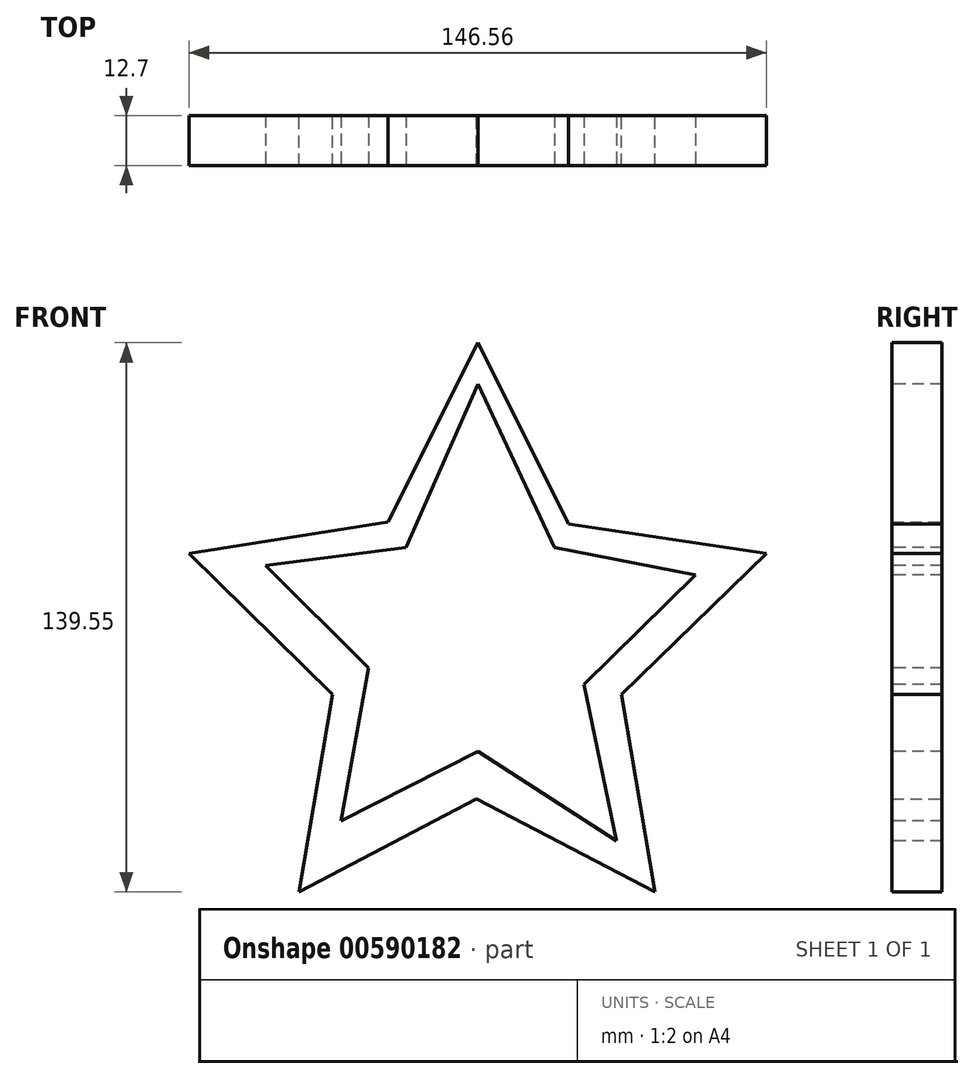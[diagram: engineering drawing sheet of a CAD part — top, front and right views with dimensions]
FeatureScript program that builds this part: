
annotation { "Feature Type Name" : "Feature", "Feature Type Description" : "" }
export const myFeature = defineFeature(function(context is Context, id is Id, definition is map)
    precondition{}
    {
        {
            var Q0;
            Q0=qCreatedBy(makeId("Front.planeOp"),FACE);
            var sketch = newSketch(context, id + "F0", { "sketchPlane" : qUnion([Q0])});
            skLineSegment(sketch, "E0", {"start": v(-16.38, 0) * mm, "end": v(-39.2, -45.54) * mm});
            skLineSegment(sketch, "E1", {"start": v(-39.2, -45.54) * mm, "end": v(-89.66, -53.55) * mm});
            skLineSegment(sketch, "E2", {"start": v(-89.66, -53.55) * mm, "end": v(-53.23, -89.36) * mm});
            skLineSegment(sketch, "E3", {"start": v(-53.23, -89.36) * mm, "end": v(-61.75, -139.55) * mm});
            skLineSegment(sketch, "E4", {"start": v(-61.75, -139.55) * mm, "end": v(-16.67, -115.9) * mm});
            skLineSegment(sketch, "E5", {"start": v(-16.67, -115.9) * mm, "end": v(28.66, -139.55) * mm});
            skLineSegment(sketch, "E6", {"start": v(28.66, -139.55) * mm, "end": v(20.14, -89.36) * mm});
            skLineSegment(sketch, "E7", {"start": v(20.14, -89.36) * mm, "end": v(56.9, -53.55) * mm});
            skLineSegment(sketch, "E8", {"start": v(56.9, -53.55) * mm, "end": v(6.62, -46.04) * mm});
            skLineSegment(sketch, "E9", {"start": v(6.62, -46.04) * mm, "end": v(-16.38, 0) * mm});
            skSolve(sketch);
        }
        {
            var Q0;
            Q0=qSketchRegion(id+"F0",true);
            extrude(context, id + "F1", {"entities" : qUnion([Q0]), "depth" : 12.7 * mm, "offsetDistance" : 25.4 * mm});
        }
        {
            var Q0;
            Q0=makeQuery(id+"F1.opExtrude","CAP_FACE",FACE,{"disambiguationData":[OSD([sQuery(id+"F0.wireOp",EDGE,"E0"),sQuery(id+"F0.wireOp",EDGE,"E1"),sQuery(id+"F0.wireOp",EDGE,"E2"),sQuery(id+"F0.wireOp",EDGE,"E3"),sQuery(id+"F0.wireOp",EDGE,"E4"),sQuery(id+"F0.wireOp",EDGE,"E5"),sQuery(id+"F0.wireOp",EDGE,"E6"),sQuery(id+"F0.wireOp",EDGE,"E7"),sQuery(id+"F0.wireOp",EDGE,"E8"),sQuery(id+"F0.wireOp",EDGE,"E9")])],"isStart":false});
            var sketch = newSketch(context, id + "F2", { "sketchPlane" : qUnion([Q0])});
            skLineSegment(sketch, "E10", {"start": v(-16.27, -10.52) * mm, "end": v(-34.59, -52.01) * mm});
            skLineSegment(sketch, "E11", {"start": v(-34.59, -52.01) * mm, "end": v(-70.34, -56.65) * mm});
            skLineSegment(sketch, "E12", {"start": v(-70.34, -56.65) * mm, "end": v(-44.07, -82.69) * mm});
            skLineSegment(sketch, "E13", {"start": v(-44.07, -82.69) * mm, "end": v(-51.14, -121.53) * mm});
            skLineSegment(sketch, "E14", {"start": v(-51.14, -121.53) * mm, "end": v(-16.38, -103.87) * mm});
            skLineSegment(sketch, "E15", {"start": v(-16.38, -103.87) * mm, "end": v(18.82, -126.6) * mm});
            skLineSegment(sketch, "E16", {"start": v(18.82, -126.6) * mm, "end": v(10.65, -86.88) * mm});
            skLineSegment(sketch, "E17", {"start": v(10.65, -86.88) * mm, "end": v(38.9, -59.07) * mm});
            skLineSegment(sketch, "E18", {"start": v(38.9, -59.07) * mm, "end": v(3.15, -52.01) * mm});
            skLineSegment(sketch, "E19", {"start": v(3.15, -52.01) * mm, "end": v(-16.27, -10.52) * mm});
            skSolve(sketch);
        }
        {
            var Q0;
            Q0=qSketchRegion(id+"F2",true);
            extrude(context, id + "F3", {"entities" : qUnion([Q0]), "oppositeDirection" : true, "depth" : 12.7 * mm, "offsetDistance" : 25.4 * mm});
        }
    });
